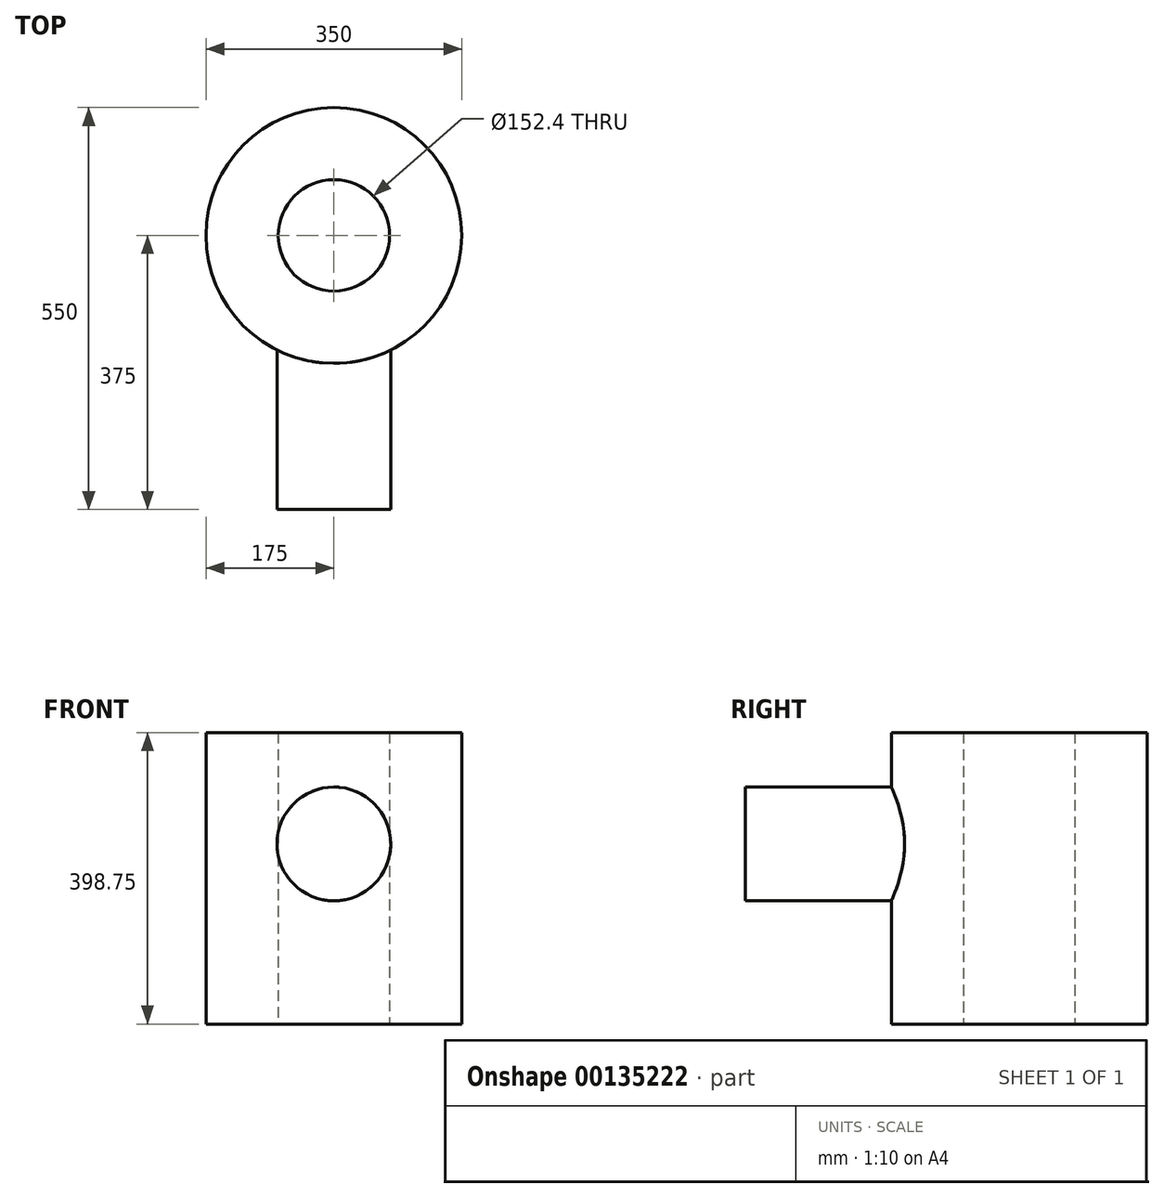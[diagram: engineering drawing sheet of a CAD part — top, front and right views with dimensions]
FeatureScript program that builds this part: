
annotation { "Feature Type Name" : "Feature", "Feature Type Description" : "" }
export const myFeature = defineFeature(function(context is Context, id is Id, definition is map)
    precondition{}
    {
        {
            var Q0;
            Q0=qCreatedBy(makeId("Top.planeOp"),FACE);
            var sketch = newSketch(context, id + "F0", { "sketchPlane" : qUnion([Q0])});
            skCircle(sketch, "E0", {"center": v(0, 0) * mm, "radius": 175 * mm});
            skSolve(sketch);
        }
        {
            var Q0;
            Q0 = qSketchRegion(id + "F0", true);
            extrude(context, id + "F1", {"entities" : qUnion([Q0]), "depth" : 398.75 * mm});
        }
        {
            var Q0;
            Q0=makeQuery(id+"F1.opExtrude","CAP_FACE",FACE,{"disambiguationData":[OSD([sQuery(id+"F0.wireOp",EDGE,"E0")])],"isStart":true});
            var sketch = newSketch(context, id + "F2", { "sketchPlane" : qUnion([Q0])});
            skCircle(sketch, "E1", {"center": v(0, 0) * mm, "radius": 76.2 * mm});
            skSolve(sketch);
        }
        {
            var Q0;
            Q0 = qSketchRegion(id + "F2", true);
            extrude(context, id + "F3", {"entities" : qUnion([Q0]), "operationType" : NewBodyOperationType.REMOVE, "endBound" : BoundingType.THROUGH_ALL, "oppositeDirection" : true, "depth" : 25 * mm});
        }
        {
            var Q0;
            Q0=qCreatedBy(makeId("Front.planeOp"),FACE);
            cPlane(context, id + "F4", {"entities" : qUnion([Q0]), "cplaneType" : CPlaneType.OFFSET, "offset" : 175 * mm, "width" : 150 * mm, "height" : 150 * mm});
        }
        {
            var Q0;
            Q0=qCreatedBy(id+"F4.planeOp",FACE);
            var sketch = newSketch(context, id + "F5", { "sketchPlane" : qUnion([Q0])});
            skCircle(sketch, "E2", {"center": v(0, 246.35) * mm, "radius": 77.85 * mm});
            skSolve(sketch);
        }
        {
            var Q0;
            Q0 = qSketchRegion(id + "F5", true);
            var Q1;
            Q1=makeQuery(id+"F1.opExtrude","SWEPT_FACE",FACE,{"disambiguationData":[OSD([sQuery(id+"F0.wireOp",EDGE,"E0")])]});
            extrude(context, id + "F6", {"entities" : qUnion([Q0]), "operationType" : NewBodyOperationType.ADD, "endBound" : BoundingType.UP_TO_SURFACE, "oppositeDirection" : true, "endBoundEntityFace" : qUnion([Q1]), "depth" : 25 * mm, "hasSecondDirection" : true, "secondDirectionOppositeDirection" : false, "secondDirectionDepth" : 200 * mm});
        }
        {
            var Q0;
            Q0=qCreatedBy(makeId("Front.planeOp"),FACE);
            cPlane(context, id + "F7", {"entities" : qUnion([Q0]), "cplaneType" : CPlaneType.OFFSET, "offset" : 95 * mm, "oppositeDirection" : true, "width" : 150 * mm, "height" : 150 * mm});
        }
        {
            var Q0;
            Q0=qCreatedBy(makeId("Right.planeOp"),FACE);
            var Q1;
            Q1=qCreatedBy(id+"F7.planeOp",FACE);
            cPlane(context, id + "F8", {"entities" : qUnion([Q0, Q1]), "cplaneType" : CPlaneType.MID_PLANE, "offset" : 25 * mm, "flipAlignment" : true, "width" : 150 * mm, "height" : 150 * mm});
        }
    });
